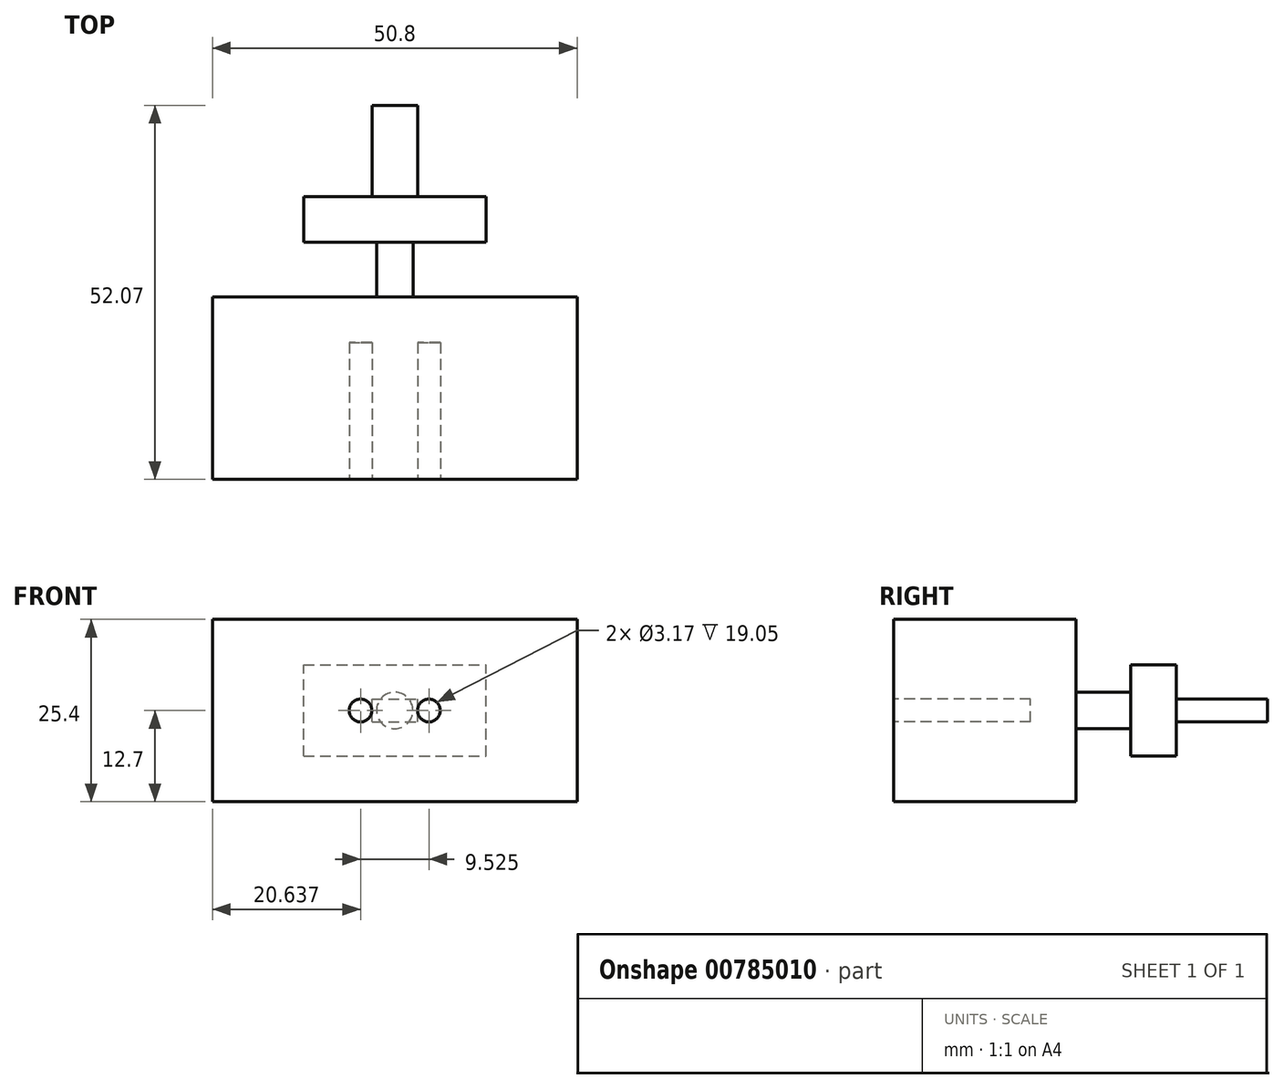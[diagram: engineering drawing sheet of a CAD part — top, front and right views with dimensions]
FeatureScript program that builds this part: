
annotation { "Feature Type Name" : "Feature", "Feature Type Description" : "" }
export const myFeature = defineFeature(function(context is Context, id is Id, definition is map)
    precondition{}
    {
        {
            var Q0;
            Q0=qCreatedBy(makeId("Front.planeOp"),FACE);
            var sketch = newSketch(context, id + "F0", { "sketchPlane" : qUnion([Q0])});
            skLineSegment(sketch, "E0.bottom", {"start": v(25.4, -12.7) * mm, "end": v(-25.4, -12.7) * mm});
            skLineSegment(sketch, "E0.top", {"start": v(25.4, 12.7) * mm, "end": v(-25.4, 12.7) * mm});
            skLineSegment(sketch, "E0.left", {"start": v(25.4, -12.7) * mm, "end": v(25.4, 12.7) * mm});
            skLineSegment(sketch, "E0.right", {"start": v(-25.4, -12.7) * mm, "end": v(-25.4, 12.7) * mm});
            skPoint(sketch, "E0.middle", {"position": v(0, 0) * mm});
            skCircle(sketch, "E1", {"center": v(4.76, 0) * mm, "radius": 1.59 * mm});
            skCircle(sketch, "E2", {"center": v(-4.76, 0) * mm, "radius": 1.59 * mm});
            skSolve(sketch);
        }
        {
            var Q0;
            Q0=qSketchRegion(id+"F0",true);
            var Q1;
            Q1=makeQuery(id+"F0.imprint","IMPRINT",FACE,{"disambiguationData":[TD([[makeQuery(id+"F0.imprint","IMPRINT",EDGE,{"derivedFrom":sQuery(id+"F0.wireOp",EDGE,"E1")}),1.0]])]});
            var Q2;
            Q2=makeQuery(id+"F0.imprint","IMPRINT",FACE,{"disambiguationData":[TD([[makeQuery(id+"F0.imprint","IMPRINT",EDGE,{"derivedFrom":sQuery(id+"F0.wireOp",EDGE,"E2")}),1.0]])]});
            extrude(context, id + "F1", {"entities" : qUnion([Q0, Q1, Q2]), "oppositeDirection" : true, "depth" : 25.4 * mm, "offsetDistance" : 25.4 * mm});
        }
        {
            var Q0;
            Q0=makeQuery(id+"F1.opExtrude","CAP_FACE",FACE,{"disambiguationData":[OSD([sQuery(id+"F0.wireOp",EDGE,"E0.bottom"),sQuery(id+"F0.wireOp",EDGE,"E0.top"),sQuery(id+"F0.wireOp",EDGE,"E0.left"),sQuery(id+"F0.wireOp",EDGE,"E0.right")])],"isStart":false});
            var sketch = newSketch(context, id + "F2", { "sketchPlane" : qUnion([Q0])});
            skCircle(sketch, "E3", {"center": v(0, 0) * mm, "radius": 2.54 * mm});
            skSolve(sketch);
        }
        {
            var Q0;
            Q0=makeQuery(id+"F2.imprint","IMPRINT",FACE,{"disambiguationData":[TD([[makeQuery(id+"F2.imprint","IMPRINT",EDGE,{"derivedFrom":sQuery(id+"F2.wireOp",EDGE,"E3")}),1.0]])]});
            extrude(context, id + "F3", {"entities" : qUnion([Q0]), "operationType" : NewBodyOperationType.ADD, "depth" : 7.62 * mm, "offsetDistance" : 25.4 * mm});
        }
        {
            var Q0;
            Q0=makeQuery(id+"F3.opExtrude","CAP_FACE",FACE,{"disambiguationData":[OSD([sQuery(id+"F2.wireOp",EDGE,"E3")])],"isStart":false});
            var sketch = newSketch(context, id + "F4", { "sketchPlane" : qUnion([Q0])});
            skLineSegment(sketch, "E4.bottom", {"start": v(12.7, -6.35) * mm, "end": v(-12.7, -6.35) * mm});
            skLineSegment(sketch, "E4.top", {"start": v(12.7, 6.35) * mm, "end": v(-12.7, 6.35) * mm});
            skLineSegment(sketch, "E4.left", {"start": v(12.7, -6.35) * mm, "end": v(12.7, 6.35) * mm});
            skLineSegment(sketch, "E4.right", {"start": v(-12.7, -6.35) * mm, "end": v(-12.7, 6.35) * mm});
            skPoint(sketch, "E4.middle", {"position": v(0, 0) * mm});
            skSolve(sketch);
        }
        {
            var Q0;
            Q0=qSketchRegion(id+"F4",true);
            extrude(context, id + "F5", {"entities" : qUnion([Q0]), "operationType" : NewBodyOperationType.ADD, "depth" : 6.35 * mm, "offsetDistance" : 25.4 * mm});
        }
        {
            var Q0;
            Q0=makeQuery(id+"F5.opExtrude","CAP_FACE",FACE,{"disambiguationData":[OSD([sQuery(id+"F4.wireOp",EDGE,"E4.bottom"),sQuery(id+"F4.wireOp",EDGE,"E4.top"),sQuery(id+"F4.wireOp",EDGE,"E4.left"),sQuery(id+"F4.wireOp",EDGE,"E4.right")])],"isStart":false});
            var sketch = newSketch(context, id + "F6", { "sketchPlane" : qUnion([Q0])});
            skLineSegment(sketch, "E5.bottom", {"start": v(3.17, -1.59) * mm, "end": v(-3.18, -1.59) * mm});
            skLineSegment(sketch, "E5.top", {"start": v(3.17, 1.59) * mm, "end": v(-3.18, 1.59) * mm});
            skLineSegment(sketch, "E5.left", {"start": v(3.17, -1.59) * mm, "end": v(3.17, 1.59) * mm});
            skLineSegment(sketch, "E5.right", {"start": v(-3.18, -1.59) * mm, "end": v(-3.18, 1.59) * mm});
            skPoint(sketch, "E5.middle", {"position": v(0, 0) * mm});
            skSolve(sketch);
        }
        {
            var Q0;
            Q0=makeQuery(id+"F6.imprint","IMPRINT",FACE,{"disambiguationData":[TD([[makeQuery(id+"F6.imprint","IMPRINT",EDGE,{"derivedFrom":sQuery(id+"F6.wireOp",EDGE,"E5.bottom")}),-1.0]])]});
            extrude(context, id + "F7", {"entities" : qUnion([Q0]), "operationType" : NewBodyOperationType.ADD, "depth" : 12.7 * mm, "offsetDistance" : 25.4 * mm});
        }
        {
            var Q0;
            Q0=makeQuery(id+"F0.imprint","IMPRINT",FACE,{"disambiguationData":[TD([[makeQuery(id+"F0.imprint","IMPRINT",EDGE,{"derivedFrom":sQuery(id+"F0.wireOp",EDGE,"E1")}),1.0]])]});
            var Q1;
            Q1=makeQuery(id+"F0.imprint","IMPRINT",FACE,{"disambiguationData":[TD([[makeQuery(id+"F0.imprint","IMPRINT",EDGE,{"derivedFrom":sQuery(id+"F0.wireOp",EDGE,"E2")}),1.0]])]});
            extrude(context, id + "F8", {"entities" : qUnion([Q0, Q1]), "operationType" : NewBodyOperationType.REMOVE, "oppositeDirection" : true, "depth" : 19.05 * mm, "offsetDistance" : 25.4 * mm});
        }
    });
